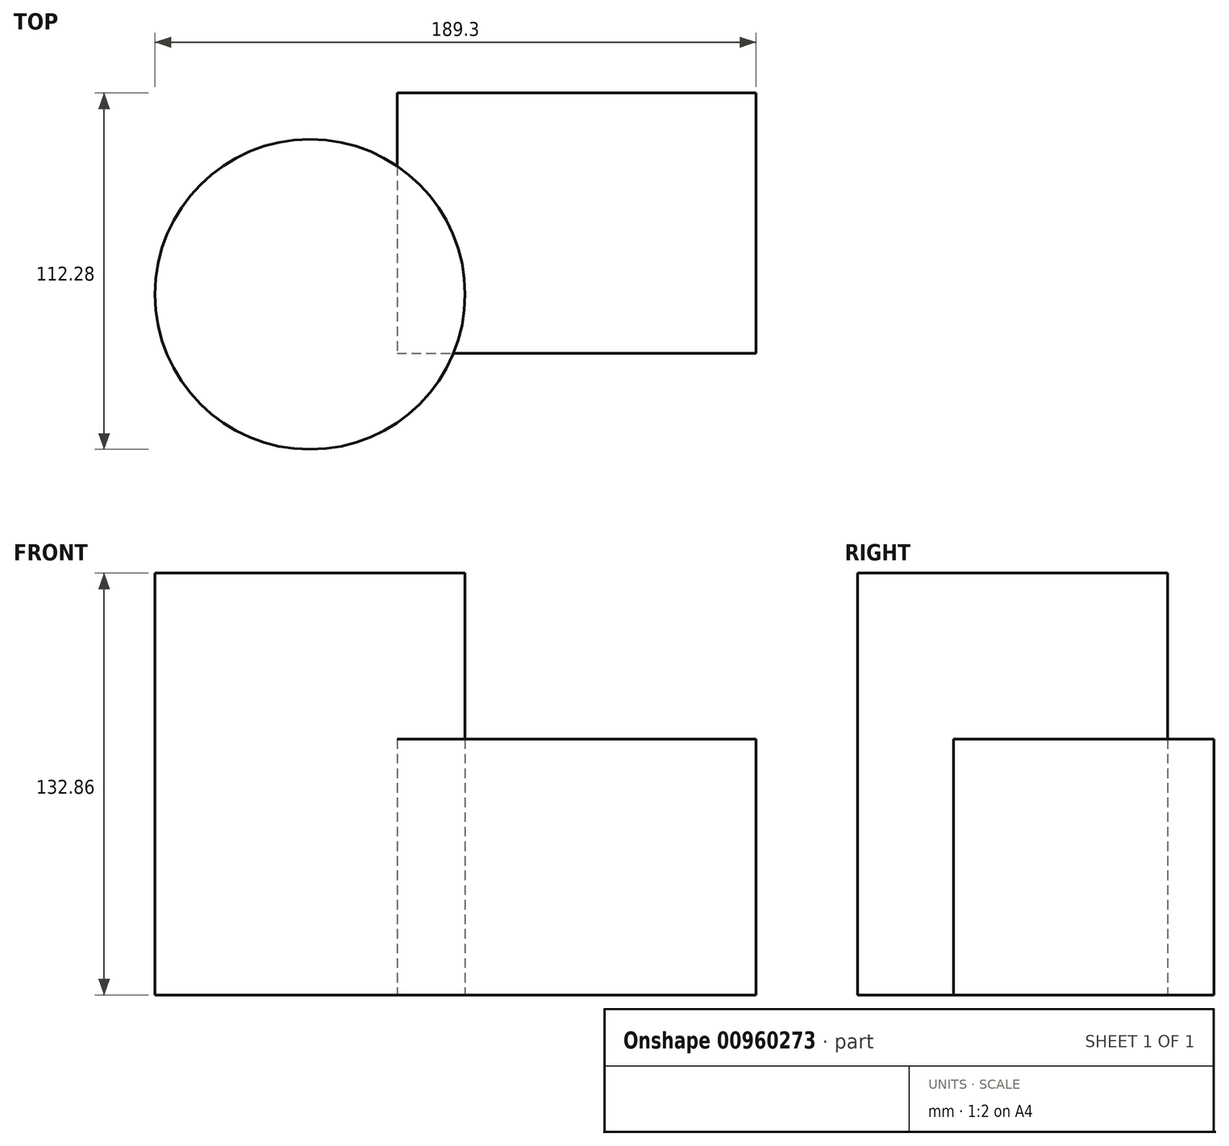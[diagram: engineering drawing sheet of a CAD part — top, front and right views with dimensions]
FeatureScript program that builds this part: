
annotation { "Feature Type Name" : "Feature", "Feature Type Description" : "" }
export const myFeature = defineFeature(function(context is Context, id is Id, definition is map)
    precondition{}
    {
        {
            var Q0;
            Q0=qCreatedBy(makeId("Top.planeOp"),FACE);
            var sketch = newSketch(context, id + "F0", { "sketchPlane" : qUnion([Q0])});
            skLineSegment(sketch, "E0.bottom", {"start": v(-57.35, 39.91) * mm, "end": v(55.7, 39.91) * mm});
            skLineSegment(sketch, "E0.top", {"start": v(-57.35, -42.07) * mm, "end": v(55.7, -42.07) * mm});
            skLineSegment(sketch, "E0.left", {"start": v(-57.35, 39.91) * mm, "end": v(-57.35, -42.07) * mm});
            skLineSegment(sketch, "E0.right", {"start": v(55.7, 39.91) * mm, "end": v(55.7, -42.07) * mm});
            skSolve(sketch);
        }
        {
            var Q0;
            Q0=makeQuery(id+"F0.imprint","IMPRINT",FACE,{"disambiguationData":[TD([[makeQuery(id+"F0.imprint","IMPRINT",EDGE,{"derivedFrom":sQuery(id+"F0.wireOp",EDGE,"E0.bottom")}),-1.0]])]});
            extrude(context, id + "F1", {"entities" : qUnion([Q0]), "depth" : 80.53 * mm, "offsetDistance" : 25.4 * mm});
        }
        {
            var Q0;
            Q0=qCreatedBy(makeId("Top.planeOp"),FACE);
            var sketch = newSketch(context, id + "F2", { "sketchPlane" : qUnion([Q0])});
            skCircle(sketch, "E1", {"center": v(-84.75, -23.52) * mm, "radius": 48.85 * mm});
            skSolve(sketch);
        }
        {
            var Q0;
            Q0 = qSketchRegion(id + "F2", true);
            var Q1;
            Q1=makeQuery(id+"F2.imprint","IMPRINT",FACE,{"disambiguationData":[TD([[makeQuery(id+"F2.imprint","IMPRINT",EDGE,{"derivedFrom":sQuery(id+"F2.wireOp",EDGE,"E1")}),1.0]])]});
            extrude(context, id + "F3", {"entities" : qUnion([Q0, Q1]), "depth" : 132.86 * mm, "offsetDistance" : 25.4 * mm});
        }
    });
